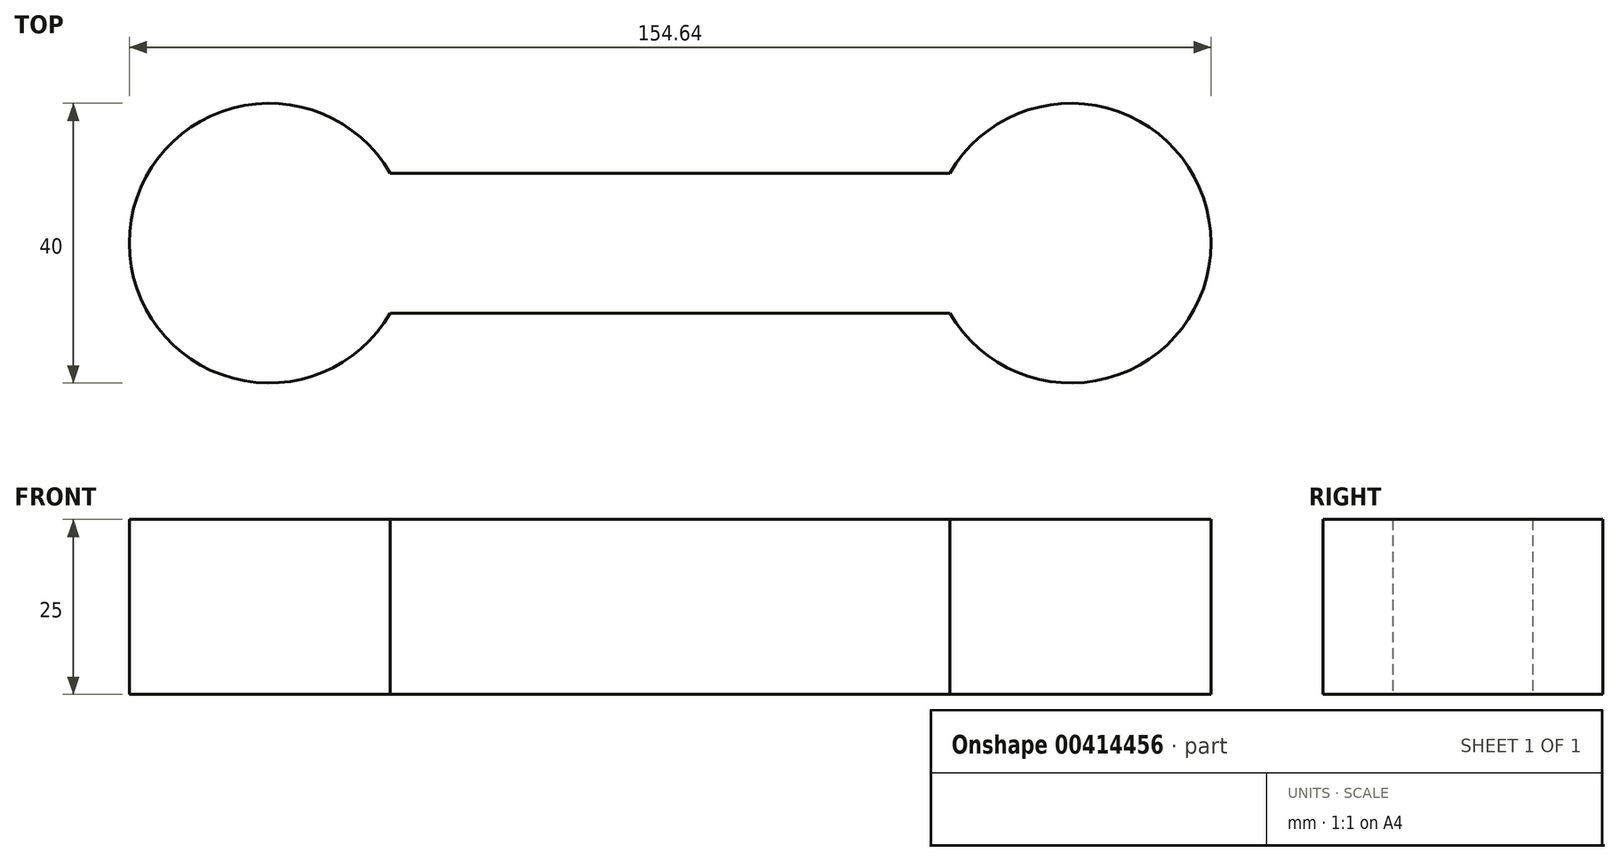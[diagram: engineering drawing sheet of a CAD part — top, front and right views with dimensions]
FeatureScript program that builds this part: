
annotation { "Feature Type Name" : "Feature", "Feature Type Description" : "" }
export const myFeature = defineFeature(function(context is Context, id is Id, definition is map)
    precondition{}
    {
        {
            var Q0;
            Q0=qCreatedBy(makeId("Top.planeOp"),FACE);
            var sketch = newSketch(context, id + "F0", { "sketchPlane" : qUnion([Q0])});
            skLineSegment(sketch, "E0.bottom", {"start": v(-43.9, 5.45) * mm, "end": v(46.1, 5.45) * mm});
            skLineSegment(sketch, "E0.top", {"start": v(-43.9, -14.55) * mm, "end": v(46.1, -14.55) * mm});
            skArc(sketch, "E1", {"start": v(-38.9, 5.45) * mm, "mid": v(-76.21, -4.55) * mm, "end": v(-38.9, -14.55) * mm});
            skArc(sketch, "E2", {"start": v(41.1, -14.55) * mm, "mid": v(78.43, -4.55) * mm, "end": v(41.1, 5.45) * mm});
            skPoint(sketch, "E3.end.orphan", {"position": v(-38.9, 27.08) * mm});
            skPoint(sketch, "E3.start.orphan", {"position": v(-43.9, 27.08) * mm});
            skPoint(sketch, "E4.end.orphan", {"position": v(41.1, 21.41) * mm});
            skPoint(sketch, "E4.start.orphan", {"position": v(46.1, 21.41) * mm});
            skSolve(sketch);
        }
        {
            var Q0;
            {var subQ0=sQuery(id+"F0.wireOp",EDGE,"E1");Q0=makeQuery(id+"F0.imprint","IMPRINT",FACE,{"disambiguationData":[TD([[makeQuery(id+"F0.imprint","IMPRINT",EDGE,{"derivedFrom":subQ0}),1.0]])]});}
            extrude(context, id + "F1", {"entities" : qUnion([Q0]), "depth" : 25 * mm});
        }
    });
